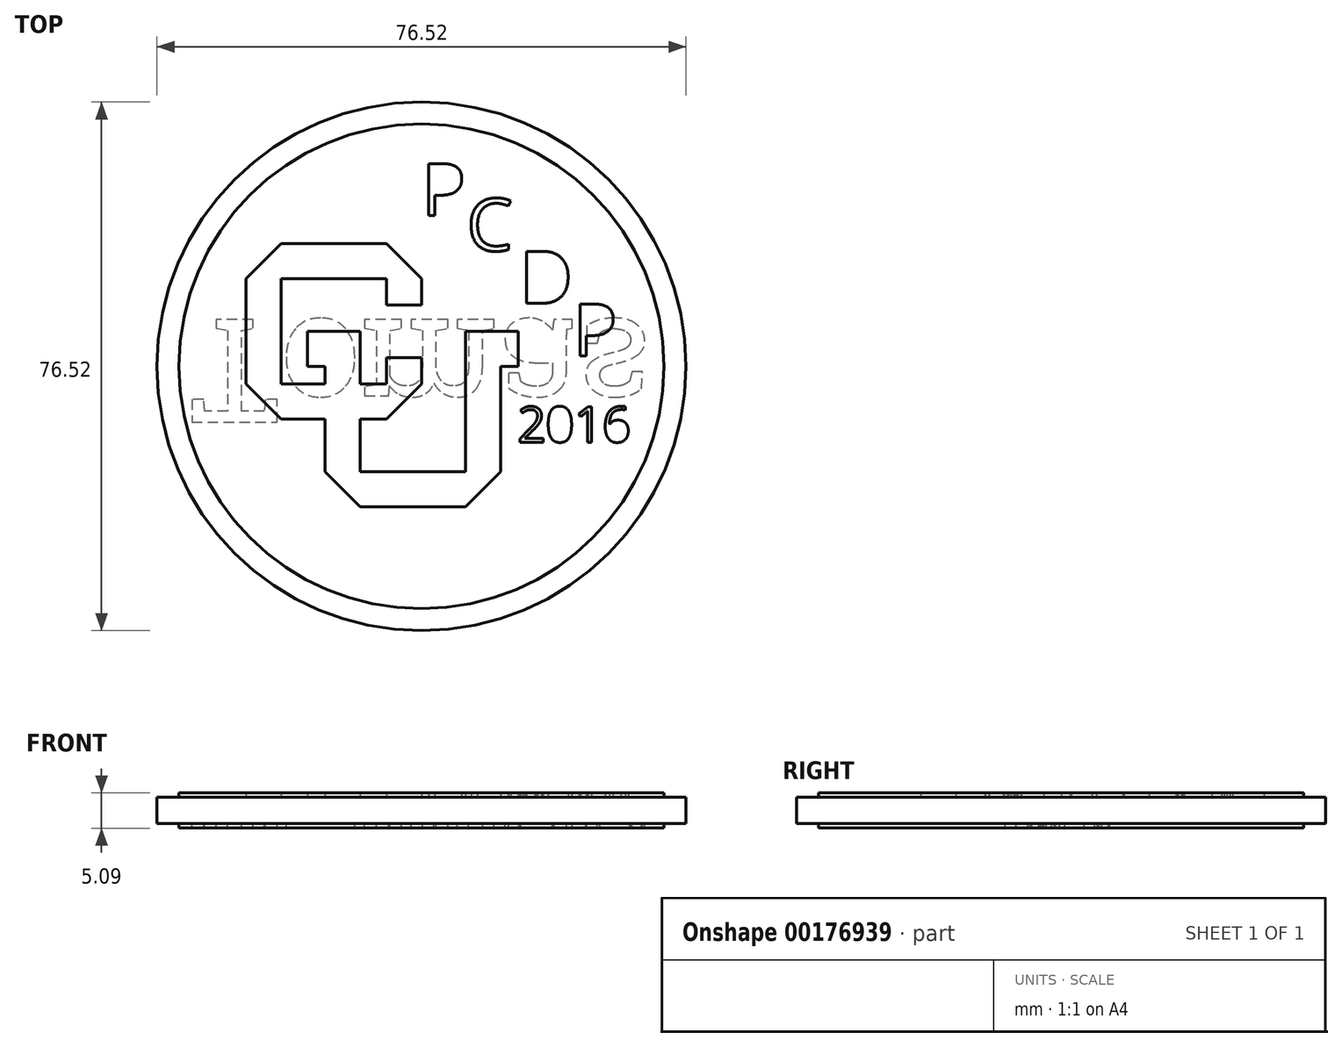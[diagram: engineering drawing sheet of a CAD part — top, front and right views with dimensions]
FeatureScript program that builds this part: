
annotation { "Feature Type Name" : "Feature", "Feature Type Description" : "" }
export const myFeature = defineFeature(function(context is Context, id is Id, definition is map)
    precondition{}
    {
        {
            var Q0;
            Q0=qCreatedBy(makeId("Top.planeOp"),FACE);
            var sketch = newSketch(context, id + "F0", { "sketchPlane" : qUnion([Q0])});
            skCircle(sketch, "E0", {"center": v(0, 0) * mm, "radius": 38.26 * mm});
            skSolve(sketch);
        }
        {
            var Q0;
            Q0=makeQuery(id+"F0.imprint","IMPRINT",FACE,{"disambiguationData":[TD([[makeQuery(id+"F0.imprint","IMPRINT",EDGE,{"derivedFrom":sQuery(id+"F0.wireOp",EDGE,"E0")}),1.0]])]});
            extrude(context, id + "F1", {"entities" : qUnion([Q0]), "depth" : 3.8 * mm});
        }
        {
            var Q0;
            Q0=makeQuery(id+"F1.opExtrude","CAP_FACE",FACE,{"disambiguationData":[OSD([sQuery(id+"F0.wireOp",EDGE,"E0")])],"isStart":false});
            var sketch = newSketch(context, id + "F2", { "sketchPlane" : qUnion([Q0])});
            skLineSegment(sketch, "E1", {"start": v(0, -2.54) * mm, "end": v(-5.08, -7.62) * mm});
            skLineSegment(sketch, "E2", {"start": v(-5.08, -7.62) * mm, "end": v(-8.9, -7.62) * mm});
            skLineSegment(sketch, "E3", {"start": v(-20.32, -7.62) * mm, "end": v(-25.4, -2.54) * mm});
            skLineSegment(sketch, "E4", {"start": v(-25.4, -2.54) * mm, "end": v(-25.4, 12.7) * mm});
            skLineSegment(sketch, "E5", {"start": v(-25.4, 12.7) * mm, "end": v(-20.32, 17.78) * mm});
            skLineSegment(sketch, "E6", {"start": v(-20.32, 17.78) * mm, "end": v(-5.08, 17.78) * mm});
            skLineSegment(sketch, "E7", {"start": v(-5.08, 17.78) * mm, "end": v(0, 12.7) * mm});
            skLineSegment(sketch, "E8", {"start": v(0, 12.7) * mm, "end": v(0, 8.89) * mm});
            skLineSegment(sketch, "E9", {"start": v(0, 8.89) * mm, "end": v(-5.08, 8.89) * mm});
            skLineSegment(sketch, "E10", {"start": v(-5.08, 8.89) * mm, "end": v(-5.08, 12.7) * mm});
            skLineSegment(sketch, "E11", {"start": v(-5.08, 12.7) * mm, "end": v(-20.32, 12.7) * mm});
            skLineSegment(sketch, "E12", {"start": v(-20.32, 12.7) * mm, "end": v(-20.32, -2.54) * mm});
            skLineSegment(sketch, "E13", {"start": v(-20.32, -2.54) * mm, "end": v(-13.97, -2.54) * mm});
            skLineSegment(sketch, "E14", {"start": v(-5.08, -2.54) * mm, "end": v(-5.08, 1.27) * mm});
            skLineSegment(sketch, "E15", {"start": v(-5.08, 1.27) * mm, "end": v(0, 1.27) * mm});
            skLineSegment(sketch, "E16", {"start": v(0, 1.27) * mm, "end": v(0, -2.54) * mm});
            skLineSegment(sketch, "E17", {"start": v(-8.89, -2.54) * mm, "end": v(-8.9, 5.08) * mm});
            skPoint(sketch, "E17.endSnap0", {"position": v(-20.32, 5.08) * mm});
            skLineSegment(sketch, "E18", {"start": v(-8.9, 5.08) * mm, "end": v(-16.5, 5.08) * mm});
            skLineSegment(sketch, "E19", {"start": v(-16.51, 5.08) * mm, "end": v(-16.5, 0) * mm});
            skLineSegment(sketch, "E20", {"start": v(-16.5, 0) * mm, "end": v(-13.97, 0) * mm});
            skLineSegment(sketch, "E21", {"start": v(-13.97, 0) * mm, "end": v(-13.97, -2.54) * mm});
            skLineSegment(sketch, "E22.trimOffspring", {"start": v(-8.9, -2.54) * mm, "end": v(-5.08, -2.54) * mm});
            skLineSegment(sketch, "E23", {"start": v(-13.97, -7.62) * mm, "end": v(-13.97, -15.24) * mm});
            skLineSegment(sketch, "E24", {"start": v(-13.97, -15.24) * mm, "end": v(-8.89, -20.32) * mm});
            skLineSegment(sketch, "E25", {"start": v(-8.89, -20.32) * mm, "end": v(6.35, -20.32) * mm});
            skLineSegment(sketch, "E26", {"start": v(6.35, -20.32) * mm, "end": v(11.43, -15.24) * mm});
            skLineSegment(sketch, "E27", {"start": v(11.43, -15.24) * mm, "end": v(11.43, -2.54) * mm});
            skLineSegment(sketch, "E28", {"start": v(11.43, 0) * mm, "end": v(13.97, 0) * mm});
            skLineSegment(sketch, "E29", {"start": v(13.97, 5.08) * mm, "end": v(6.35, 5.08) * mm});
            skLineSegment(sketch, "E30", {"start": v(6.35, 5.08) * mm, "end": v(6.35, -15.24) * mm});
            skLineSegment(sketch, "E31", {"start": v(6.35, -15.24) * mm, "end": v(-8.89, -15.24) * mm});
            skLineSegment(sketch, "E32", {"start": v(-8.9, -15.24) * mm, "end": v(-8.9, -7.62) * mm});
            skLineSegment(sketch, "E33.trimOffspring", {"start": v(-13.97, -7.62) * mm, "end": v(-20.32, -7.62) * mm});
            skLineSegment(sketch, "E34", {"start": v(11.43, -2.54) * mm, "end": v(11.43, 0) * mm});
            skLineSegment(sketch, "E35", {"start": v(13.97, 0) * mm, "end": v(13.97, 5.08) * mm});
            skCircle(sketch, "E36.0", {"center": v(0, 0) * mm, "radius": 35.08 * mm});
            skText(sketch, "E37", { "text": "P", "fontName": "OpenSans-Regular.ttf"});
            skText(sketch, "E38", { "text": "C", "fontName": "OpenSans-Regular.ttf"});
            skText(sketch, "E39", { "text": "D", "fontName": "OpenSans-Regular.ttf"});
            skText(sketch, "E40", { "text": "P", "fontName": "OpenSans-Regular.ttf"});
            skText(sketch, "E41", { "text": "2016", "fontName": "OpenSans-Regular.ttf"});
            const initialGuessF2  = {"E37": [0, 0.0218, 1, 0, 0.00762], "E38": [0.00652, 0.01672, 1, 0, 0.00762], "E39": [0.01414, 0.0091, 1, 0, 0.00762], "E40": [0.0219, 0.00148, 1, 0, 0.00762], "E41": [0.01387, -0.01097, 1, 0, 0.00516]};
            skSetInitialGuess(sketch, initialGuessF2);
            skSolve(sketch);
        }
        {
            var Q0;
            Q0 = qSketchRegion(id + "F4", true);
            var Q1;
            Q1 = qSketchRegion(id + "F2", true);
            extrude(context, id + "F3", {"entities" : qUnion([Q0, Q1]), "operationType" : NewBodyOperationType.ADD, "depth" : 0.64 * mm});
        }
        {
            var Q0;
            Q0=makeQuery(id+"F1.opExtrude","CAP_FACE",FACE,{"disambiguationData":[OSD([sQuery(id+"F0.wireOp",EDGE,"E0")])],"isStart":true});
            var sketch = newSketch(context, id + "F4", { "sketchPlane" : qUnion([Q0])});
            skText(sketch, "E42", { "text": "Tomas", "fontName": "RobotoSlab-Regular.ttf"});
            skCircle(sketch, "E43.0", {"center": v(0, 0) * mm, "radius": 35.08 * mm});
            skPoint(sketch, "E44.end.orphan", {"position": v(-4.31, -21.26) * mm});
            skPoint(sketch, "E45.end.orphan", {"position": v(-5.65, -15.73) * mm});
            skPoint(sketch, "E46.start.orphan", {"position": v(-5.65, -27.75) * mm});
            skPoint(sketch, "E47.start.orphan", {"position": v(-7.56, -21.26) * mm});
            skPoint(sketch, "E48.start.orphan", {"position": v(-16.14, -27.75) * mm});
            const initialGuessF4  = {"E42": [-0.0336, -0.00679, 1, 0, 0.01507]};
            skSetInitialGuess(sketch, initialGuessF4);
            skSolve(sketch);
        }
        {
            var Q0;
            Q0 = qSketchRegion(id + "F4", true);
            extrude(context, id + "F5", {"entities" : qUnion([Q0]), "operationType" : NewBodyOperationType.ADD, "depth" : 0.64 * mm});
        }
    });
